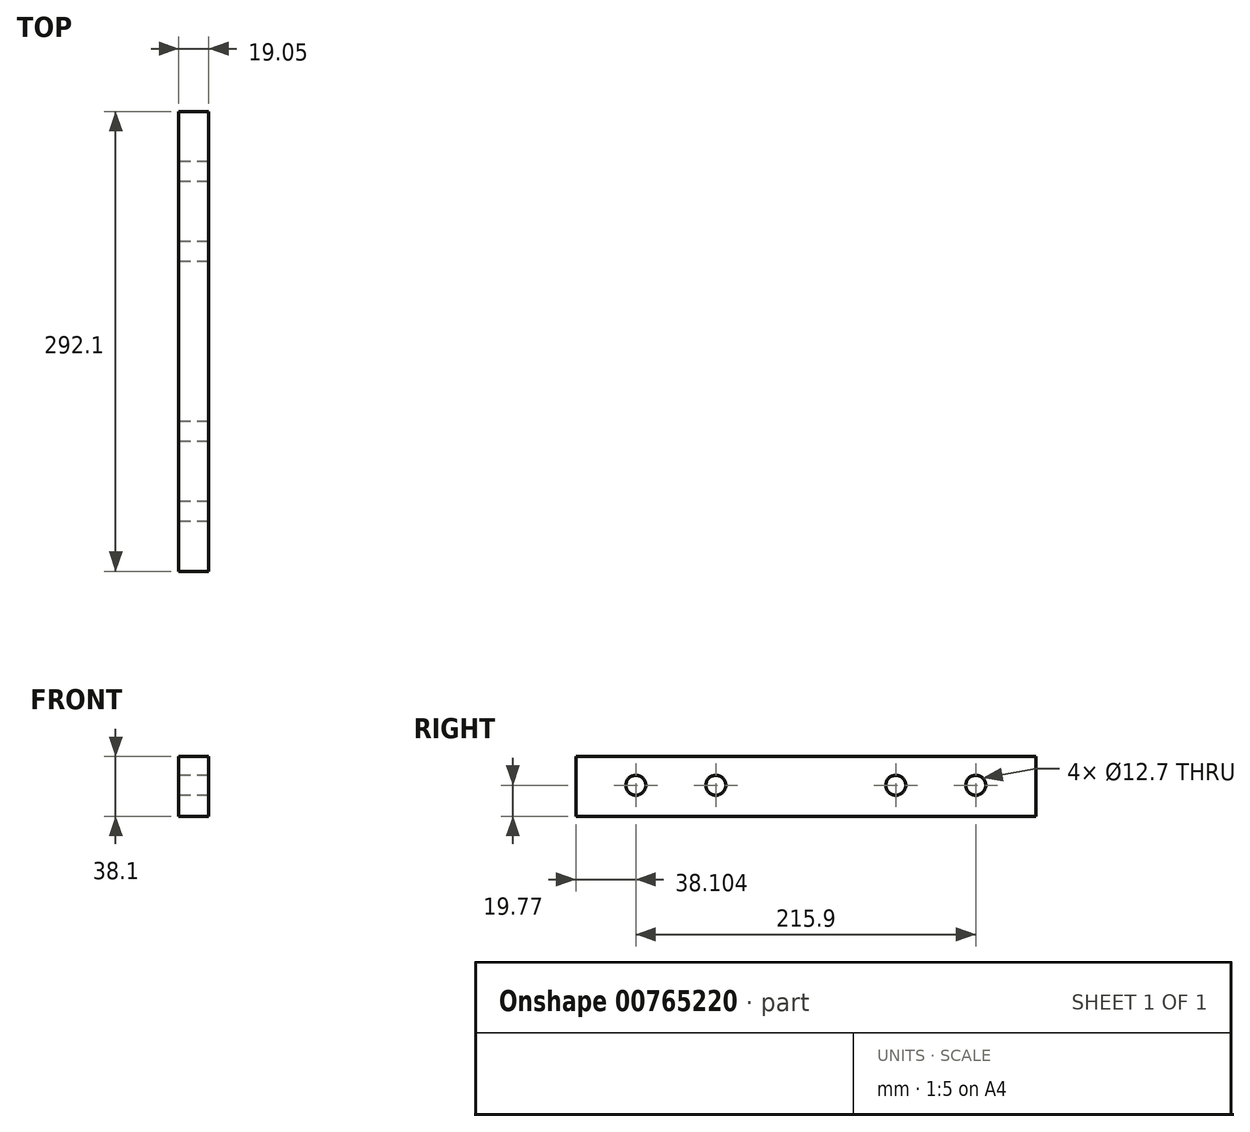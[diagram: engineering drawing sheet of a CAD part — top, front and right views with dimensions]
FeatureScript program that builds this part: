
annotation { "Feature Type Name" : "Feature", "Feature Type Description" : "" }
export const myFeature = defineFeature(function(context is Context, id is Id, definition is map)
    precondition{}
    {
        {
            var Q0;
            Q0=qCreatedBy(makeId("Right.planeOp"),FACE);
            var sketch = newSketch(context, id + "F0", { "sketchPlane" : qUnion([Q0])});
            skLineSegment(sketch, "E0.bottom", {"start": v(-23.65, 18.33) * mm, "end": v(268.45, 18.33) * mm});
            skLineSegment(sketch, "E0.top", {"start": v(-23.65, -19.77) * mm, "end": v(268.45, -19.77) * mm});
            skLineSegment(sketch, "E0.left", {"start": v(-23.65, 18.33) * mm, "end": v(-23.65, -19.77) * mm});
            skLineSegment(sketch, "E0.right", {"start": v(268.45, 18.33) * mm, "end": v(268.45, -19.77) * mm});
            skLineSegment(sketch, "E1", {"start": v(-23.65, 18.33) * mm, "end": v(14.45, 18.33) * mm, "construction": true});
            skLineSegment(sketch, "E2", {"start": v(-23.65, 18.33) * mm, "end": v(65.25, 18.33) * mm, "construction": true});
            skCircle(sketch, "E3", {"center": v(14.45, 0) * mm, "radius": 6.35 * mm});
            skCircle(sketch, "E4", {"center": v(65.25, 0) * mm, "radius": 6.35 * mm});
            skLineSegment(sketch, "E5", {"start": v(268.45, 18.33) * mm, "end": v(179.55, 18.33) * mm, "construction": true});
            skLineSegment(sketch, "E6", {"start": v(268.45, 18.33) * mm, "end": v(230.35, 18.33) * mm, "construction": true});
            skCircle(sketch, "E7", {"center": v(179.55, 0) * mm, "radius": 6.35 * mm});
            skCircle(sketch, "E8", {"center": v(230.35, 0) * mm, "radius": 6.35 * mm});
            skSolve(sketch);
        }
        {
            var Q0;
            Q0 = qSketchRegion(id + "F0", true);
            extrude(context, id + "F1", {"entities" : qUnion([Q0]), "depth" : 19.05 * mm, "offsetDistance" : 25.4 * mm});
        }
    });
